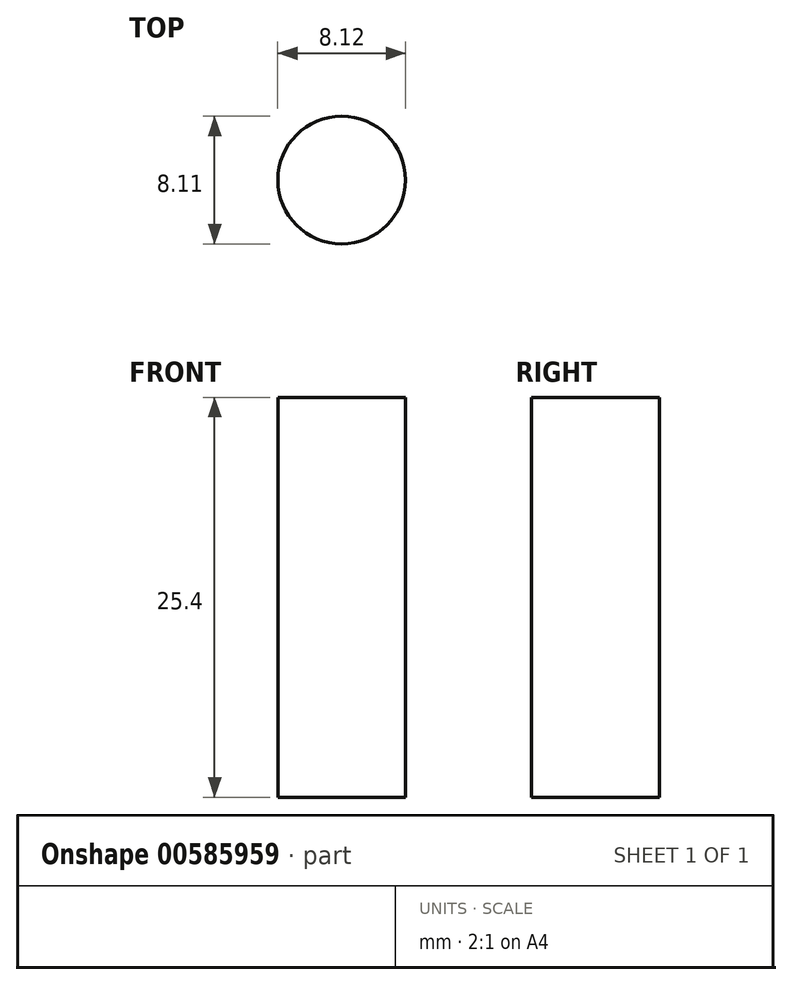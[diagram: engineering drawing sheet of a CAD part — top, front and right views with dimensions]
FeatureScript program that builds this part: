
annotation { "Feature Type Name" : "Feature", "Feature Type Description" : "" }
export const myFeature = defineFeature(function(context is Context, id is Id, definition is map)
    precondition{}
    {
        {
            var Q0;
            Q0=qCreatedBy(makeId("Top.planeOp"),FACE);
            var sketch = newSketch(context, id + "F0", { "sketchPlane" : qUnion([Q0])});
            skLineSegment(sketch, "E0.bottom", {"start": v(0, 0) * mm, "end": v(-50.9, 0) * mm});
            skLineSegment(sketch, "E0.top", {"start": v(0, 46.33) * mm, "end": v(-50.9, 46.33) * mm});
            skLineSegment(sketch, "E0.left", {"start": v(0, 0) * mm, "end": v(0, 46.33) * mm});
            skLineSegment(sketch, "E0.right", {"start": v(-50.9, 0) * mm, "end": v(-50.9, 46.33) * mm});
            skLineSegment(sketch, "E1.bottom", {"start": v(-36.73, 31.28) * mm, "end": v(-11.66, 31.28) * mm});
            skLineSegment(sketch, "E1.top", {"start": v(-36.73, 13.62) * mm, "end": v(-11.66, 13.62) * mm});
            skLineSegment(sketch, "E1.left", {"start": v(-36.73, 31.28) * mm, "end": v(-36.73, 13.62) * mm});
            skLineSegment(sketch, "E1.right", {"start": v(-11.66, 31.28) * mm, "end": v(-11.66, 13.62) * mm});
            skCircle(sketch, "E2", {"center": v(-24.1, 22.13) * mm, "radius": 4.06 * mm});
            skSolve(sketch);
        }
        {
            var Q0;
            Q0=sQuery(id+"F0.wireOp",EDGE,"E2");
            extrude(context, id + "F1", {"bodyType" : ToolBodyType.SURFACE, "surfaceEntities" : qUnion([Q0]), "depth" : 25.4 * mm, "offsetDistance" : 25.4 * mm});
        }
    });
